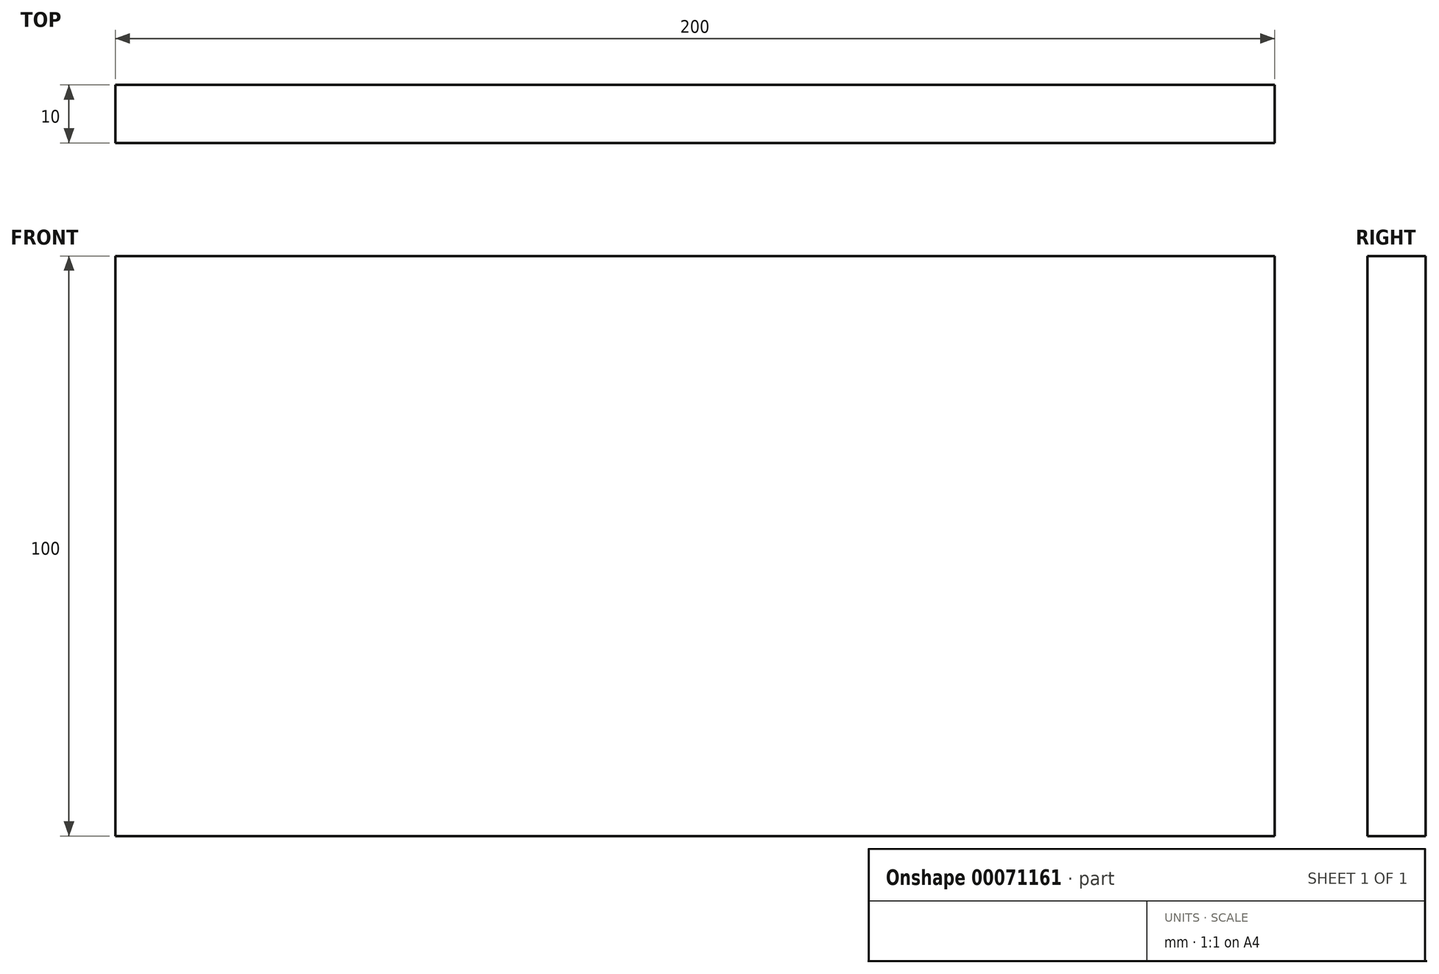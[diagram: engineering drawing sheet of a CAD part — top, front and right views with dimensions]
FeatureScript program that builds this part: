
annotation { "Feature Type Name" : "Feature", "Feature Type Description" : "" }
export const myFeature = defineFeature(function(context is Context, id is Id, definition is map)
    precondition{}
    {
        {
            var Q0;
            Q0=qCreatedBy(makeId("Front.planeOp"),FACE);
            var sketch = newSketch(context, id + "F0", { "sketchPlane" : qUnion([Q0])});
            skLineSegment(sketch, "E0.bottom", {"start": v(0, 0) * mm, "end": v(-200, 0) * mm});
            skLineSegment(sketch, "E0.top", {"start": v(0, 100) * mm, "end": v(-200, 100) * mm});
            skLineSegment(sketch, "E0.left", {"start": v(0, 0) * mm, "end": v(0, 100) * mm});
            skLineSegment(sketch, "E0.right", {"start": v(-200, 0) * mm, "end": v(-200, 100) * mm});
            skSolve(sketch);
        }
        {
            var Q0;
            Q0 = qSketchRegion(id + "F0", true);
            extrude(context, id + "F1", {"entities" : qUnion([Q0]), "depth" : 10 * mm});
        }
    });
